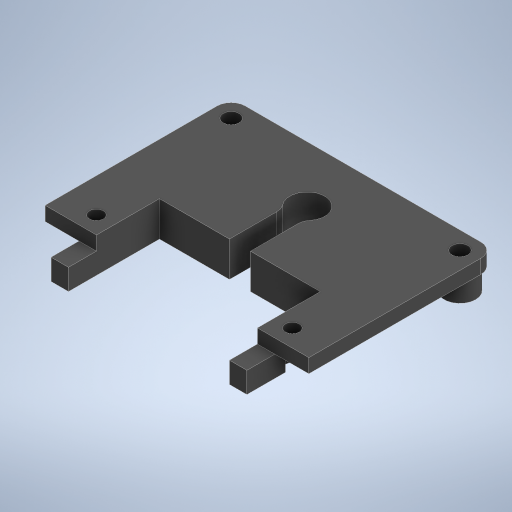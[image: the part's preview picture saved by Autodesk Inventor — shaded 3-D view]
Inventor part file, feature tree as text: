
AUTODESK INVENTOR PART (.ipt)
format: ipt  version: 2024.2 (Build 282272000, 272)  size: 415,232 bytes
history: native  units: mm
features: extrude x13, sketch x13, fillet x3, projected_geometry x2
ambient origin geometry x8: Origin, YZ Plane, XZ Plane, XY Plane, X Axis, Y Axis, Z Axis, Center Point
bodies: Solid1 (feature_tree)
feature tree (31):
  extrude  "Extrusion1"  Depth=38.5mm
  extrude  "Extrusion2"  Depth=4.0mm
  extrude  "Extrusion3"  Depth=4.0mm
  extrude  "Extrusion4"  Depth=3.0mm TaperAngle=0.0deg
  fillet  "Fillet1"  Radius=48.2mm
  extrude  "Extrusion6"  Depth=4.85mm
  extrude  "Extrusion9"  Depth=2.0mm TaperAngle=0.0deg
  extrude  "Extrusion10"  Depth=2.35mm
  fillet  "Fillet2"  Radius=2.35mm
  extrude  "Extrusion11"  Depth=2.35mm
  extrude  "Extrusion12"  Depth=4.5mm
  extrude  "Extrusion13"  Depth=4.5mm
  extrude  "Extrusion14"  Depth=2.35mm
  fillet  "Fillet3"  Radius=2.35mm
  extrude  "Extrusion15"  Depth=2.0mm
  extrude  "Extrusion17"  Depth=2.0mm
  sketch  "Sketch1"  dims[d0=28.0mm d1=38.5mm]
  sketch  "Sketch2"  dims[d6=3.0mm d7=0.0mm d8=4.0mm]
  sketch  "Sketch3"  dims[d9=4.0mm d10=4.0mm]
  sketch  "Sketch4"  dims[d11=4.0mm d12=3.0mm d13=0.0mm d14=48.2mm]
  sketch  "Sketch5"  dims[d15=37.7mm d16=4.85mm]
  sketch  "Sketch8"  dims[d17=4.85mm d18=2.0mm d19=0.0mm]
  sketch  "Sketch9"  dims[d20=4.5mm d21=2.35mm d22=2.35mm]
  sketch  "Sketch10"  dims[d23=4.5mm d24=2.35mm]
  sketch  "Sketch11"  dims[d25=2.35mm d26=4.5mm]
  sketch  "Sketch12"  dims[d27=2.35mm d28=4.5mm]
  sketch  "Sketch13"  dims[d29=2.35mm d30=2.35mm d31=2.35mm]
  sketch  "Sketch14"  dims[d32=3.0mm d33=0.0mm d34=2.0mm]
  projected_geometry  "Projected Loop1"
  projected_geometry  "Projected Loop2"
  sketch  "Sketch16"  dims[d45=2.0mm d46=2.0mm d51=0.0mm d52=0.0mm d68=3.5mm d69=3.125mm d70=18.85mm d71=0.0mm d72=0.0mm d73=28.0mm d76=2.0mm d77=1.0mm d78=0.0mm d79=0.0mm d80=2.0mm d81=24.1mm d82=4.85mm d83=23.0mm d84=13.0mm d85=7.35mm d86=6.5mm d87=0.0mm d88=0.0mm d90=0.0mm d91=0.0mm d92=5.0mm d93=3.125mm d94=18.85mm d95=0.0mm d96=0.0mm d97=3.0mm d98=0.0mm d99=0.0mm d100=2.0mm d101=2.3mm d102=2.3mm d103=0.0mm d104=0.0mm d109=4.0mm d110=4.0mm d111=2.0mm d112=0.0mm d63=0.5mm d64=0.872665mm d65=0.5mm d66=0.872665mm]
